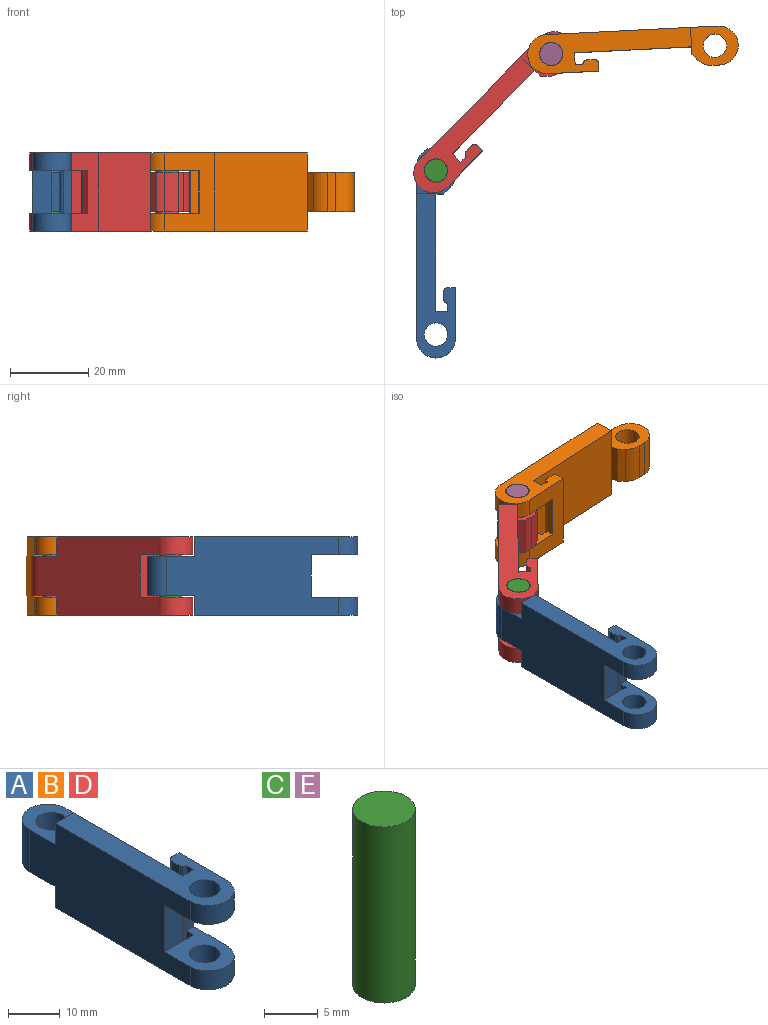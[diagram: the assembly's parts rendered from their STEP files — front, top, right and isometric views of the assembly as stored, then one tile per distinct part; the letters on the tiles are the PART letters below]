
ASSEMBLY  parts=5 mates=4
PART A: 31 faces, bbox 10x54x20 mm
  f0: plane 11x5mm, normal (0,-1,0), area 55mm2, adj f1,f2,f17,f30
  f1: plane 44x20mm, normal (-1,0,0), area 733mm2, adj f0,f3,f4,f9,f11,f15,f17,f23
  f2: plane 30x20mm, normal (1,0,0), area 600mm2, adj f0,f3,f4,f5,f12,f23,f24,f26
  f3: plane 5x5mm, normal (0,1,0), area 25mm2, adj f1,f2,f4,f11
  f4: plane 42x10mm, normal (0,0,1), area 246.6mm2, adj f1,f2,f3,f12,f13,f14,f15,f16
  f5: plane 10x2mm, normal (0,-1,0), area 20mm2, adj f2,f6,f11,f25
  f6: plane 10x1.45mm, normal (0.69,-0.72,0), area 20mm2, adj f5,f7,f11,f25
  f7: cylinder r=5mm len=10mm, axis (0,0,-1), area 40.5mm2, adj f6,f8,f11,f25
  f8: plane 10x2mm, normal (1,0,0), area 20mm2, adj f7,f9,f11,f25
  f9: cylinder r=5mm len=10mm, axis (0,0,-1), area 157.1mm2, adj f1,f8,f11,f25
  f10: cylinder r=3mm len=10mm, axis (0,0,-1), area 188.5mm2, adj f11,f25
  f11: plane 12x10mm, normal (0,0,1), area 76.1mm2, adj f1,f3,f5,f6,f7,f8,f9,f10
  f12: plane 4.5x3mm, normal (0,1,0), area 13.5mm2, adj f2,f4,f14,f17
  f13: plane 20x13mm, normal (1,0,0), area 161mm2, adj f4,f15,f17,f19,f20,f24,f28,f30
  f14: plane 4.5x2mm, normal (-1,0,0), area 9mm2, adj f4,f12,f17,f18
  f15: cylinder r=5mm len=10mm, axis (0,0,-1), area 70.7mm2, adj f1,f4,f13,f17
  f16: cylinder r=3mm len=6mm, axis (0,0,-1), area 84.8mm2, adj f4,f17
  f17: plane 14x10mm, normal (0,0,-1), area 85mm2, adj f0,f1,f12,f13,f14,f15,f16,f19
  f18: cylinder r=1mm len=20mm, axis (0,0,-1), area 31.4mm2, adj f4,f14,f19,f22,f24,f27
  f19: plane 11x2mm, normal (0,-1,0), area 22mm2, adj f13,f17,f18,f30
  f20: plane 20x2mm, normal (0,1,0), area 40mm2, adj f4,f13,f21,f24
  f21: cylinder r=1mm len=20mm, axis (0,0,-1), area 31.4mm2, adj f4,f20,f22,f24
  f22: plane 20x2mm, normal (-1,0,0), area 40mm2, adj f4,f18,f21,f24
  f23: plane 5x5mm, normal (0,1,0), area 25mm2, adj f1,f2,f24,f25
  f24: plane 42x10mm, normal (0,0,-1), area 246.6mm2, adj f1,f2,f13,f18,f20,f21,f22,f23
  f25: plane 12x10mm, normal (0,0,-1), area 76.1mm2, adj f1,f5,f6,f7,f8,f9,f10,f23
  f26: plane 4.5x3mm, normal (0,1,0), area 13.5mm2, adj f2,f24,f27,f30
  f27: plane 4.5x2mm, normal (-1,0,0), area 9mm2, adj f18,f24,f26,f30
  f28: cylinder r=5mm len=10mm, axis (0,0,1), area 70.7mm2, adj f1,f13,f24,f30
  f29: cylinder r=3mm len=6mm, axis (0,0,1), area 84.8mm2, adj f24,f30
  f30: plane 14x10mm, normal (0,0,1), area 85mm2, adj f0,f1,f13,f19,f26,f27,f28,f29
PART B: same geometry as A
PART C: 3 faces, bbox 5.8x5.8x20 mm
  f0: cylinder r=2.9mm len=20mm, axis (0,0,-1), area 364.4mm2, adj f1,f2
  f1: plane 5.8x5.8mm, normal (0,0,1), area 26.4mm2, adj f0
  f2: plane 5.8x5.8mm, normal (0,0,-1), area 26.4mm2, adj f0
PART D: same geometry as A
PART E: same geometry as C
PLACE A t=(-4.98,2.28,-1.71)mm fixed
PLACE B rot(axis=(0,0,-1),87.1deg) t=(45.51,54.23,-1.71)mm
PLACE C t=(-4.98,2.28,-1.71)mm
PLACE D rot(axis=(0,0,-1),44.7deg) t=(9.78,38.22,-1.71)mm
PLACE E rot(axis=(0,0,-1),20.7deg) t=(17.1,33.52,-1.71)mm
MATE revolute C.f0 <-> A.f10  axis (0,0,1) through (-4.98,23.28,8.29)mm
MATE revolute B.f16 <-> E.f0  axis (0,0,1) through (24.54,53.16,8.29)mm
MATE revolute D.f16 <-> A.f10  axis (0,0,-1) through (-4.98,23.28,8.29)mm
MATE revolute E.f0 <-> D.f10  axis (0,0,1) through (24.54,53.16,8.29)mm
